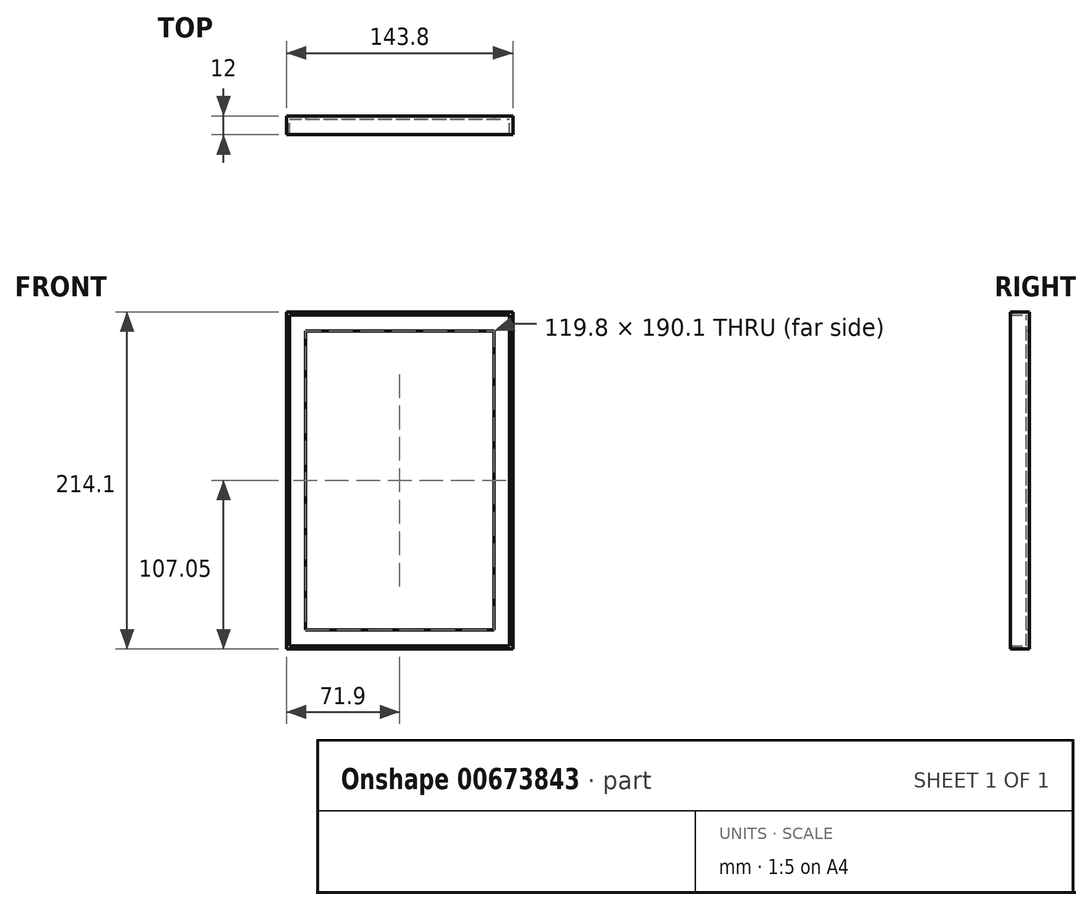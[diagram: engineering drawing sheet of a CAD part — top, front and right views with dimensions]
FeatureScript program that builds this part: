
annotation { "Feature Type Name" : "Feature", "Feature Type Description" : "" }
export const myFeature = defineFeature(function(context is Context, id is Id, definition is map)
    precondition{}
    {
        {
            var Q0;
            Q0=qCreatedBy(makeId("Front.planeOp"),FACE);
            var sketch = newSketch(context, id + "F0", { "sketchPlane" : qUnion([Q0])});
            skLineSegment(sketch, "E0.bottom", {"start": v(-145.8, -21.97) * mm, "end": v(-69, -21.97) * mm});
            skLineSegment(sketch, "E0.top", {"start": v(-145.8, 125.13) * mm, "end": v(-69, 125.13) * mm});
            skLineSegment(sketch, "E0.left", {"start": v(-145.8, -21.97) * mm, "end": v(-145.8, 125.13) * mm});
            skLineSegment(sketch, "E0.right", {"start": v(-69, -21.97) * mm, "end": v(-69, 125.13) * mm});
            skLineSegment(sketch, "E1", {"start": v(-144.8, -47.13) * mm, "end": v(-81.8, -47.13) * mm});
            skLineSegment(sketch, "E2.bottom", {"start": v(0, 0) * mm, "end": v(143.8, 0) * mm});
            skLineSegment(sketch, "E2.top", {"start": v(0, 214.1) * mm, "end": v(143.8, 214.1) * mm});
            skLineSegment(sketch, "E2.left", {"start": v(0, 0) * mm, "end": v(0, 214.1) * mm});
            skLineSegment(sketch, "E2.right", {"start": v(143.8, 0) * mm, "end": v(143.8, 214.1) * mm});
            skLineSegment(sketch, "E3.0", {"start": v(2, 212.1) * mm, "end": v(141.8, 212.1) * mm});
            skLineSegment(sketch, "E3.1", {"start": v(2, 2) * mm, "end": v(2, 212.1) * mm});
            skLineSegment(sketch, "E3.2", {"start": v(2, 2) * mm, "end": v(141.8, 2) * mm});
            skLineSegment(sketch, "E3.3", {"start": v(141.8, 2) * mm, "end": v(141.8, 212.1) * mm});
            skLineSegment(sketch, "E4", {"start": v(78.8, 212.1) * mm, "end": v(78.8, 149.1) * mm});
            skLineSegment(sketch, "E5", {"start": v(78.8, 149.1) * mm, "end": v(141.8, 149.1) * mm});
            skLineSegment(sketch, "E6", {"start": v(2, 149.1) * mm, "end": v(78.8, 149.1) * mm});
            skLineSegment(sketch, "E7", {"start": v(78.8, 149.1) * mm, "end": v(78.8, 2) * mm});
            skLineSegment(sketch, "E8.0", {"start": v(12, 202.1) * mm, "end": v(131.8, 202.1) * mm});
            skLineSegment(sketch, "E8.1", {"start": v(12, 12) * mm, "end": v(12, 202.1) * mm});
            skLineSegment(sketch, "E8.2", {"start": v(12, 12) * mm, "end": v(131.8, 12) * mm});
            skLineSegment(sketch, "E8.3", {"start": v(131.8, 12) * mm, "end": v(131.8, 202.1) * mm});
            skSolve(sketch);
        }
        {
            var Q0;
            Q0=makeQuery(id+"F0.imprint","IMPRINT",FACE,{"disambiguationData":[TD([[makeQuery(id+"F0.imprint","IMPRINT",EDGE,{"derivedFrom":sQuery(id+"F0.wireOp",EDGE,"E2.bottom")}),1.0]])]});
            extrude(context, id + "F1", {"entities" : qUnion([Q0]), "depth" : 10 * mm, "offsetDistance" : 25 * mm});
        }
        {
            var Q0;
            Q0=makeQuery(id+"F0.imprint","IMPRINT",FACE,{"disambiguationData":[TD([[makeQuery(id+"F0.imprint","IMPRINT",EDGE,{"derivedFrom":sQuery(id+"F0.wireOp",EDGE,"E2.bottom")}),1.0]])]});
            var Q1;
            {var subQ1=sQuery(id+"F0.wireOp",EDGE,"E3.1");var subQ6=sQuery(id+"F0.wireOp",EDGE,"E3.0");var subQ11=makeQuery(id+"F0.imprint","INTERSECT",VERTEX,{"derivedFrom":[subQ6,subQ1]});Q1=makeQuery(id+"F0.imprint","IMPRINT",FACE,{"disambiguationData":[TD([[makeQuery(id+"F0.imprint","IMPRINT",EDGE,{"disambiguationData":[TD([[subQ11,-1.0]])],"derivedFrom":subQ6}),-1.0]])]});}
            var Q2;
            {var subQ1=sQuery(id+"F0.wireOp",EDGE,"E3.0");var subQ5=sQuery(id+"F0.wireOp",EDGE,"E3.3");var subQ6=makeQuery(id+"F0.imprint","INTERSECT",VERTEX,{"derivedFrom":[subQ1,subQ5]});Q2=makeQuery(id+"F0.imprint","IMPRINT",FACE,{"disambiguationData":[TD([[makeQuery(id+"F0.imprint","IMPRINT",EDGE,{"disambiguationData":[TD([[subQ6,1.0]])],"derivedFrom":subQ1}),-1.0]])]});}
            var Q3;
            {var subQ1=sQuery(id+"F0.wireOp",EDGE,"E3.2");var subQ5=sQuery(id+"F0.wireOp",EDGE,"E3.1");var subQ6=makeQuery(id+"F0.imprint","INTERSECT",VERTEX,{"derivedFrom":[subQ5,subQ1]});Q3=makeQuery(id+"F0.imprint","IMPRINT",FACE,{"disambiguationData":[TD([[makeQuery(id+"F0.imprint","IMPRINT",EDGE,{"disambiguationData":[TD([[subQ6,-1.0]])],"derivedFrom":subQ5}),-1.0]])]});}
            var Q4;
            {var subQ1=sQuery(id+"F0.wireOp",EDGE,"E3.3");var subQ7=sQuery(id+"F0.wireOp",EDGE,"E3.2");var subQ8=makeQuery(id+"F0.imprint","INTERSECT",VERTEX,{"derivedFrom":[subQ7,subQ1]});Q4=makeQuery(id+"F0.imprint","IMPRINT",FACE,{"disambiguationData":[TD([[makeQuery(id+"F0.imprint","IMPRINT",EDGE,{"disambiguationData":[TD([[subQ8,1.0]])],"derivedFrom":subQ7}),1.0]])]});}
            extrude(context, id + "F2", {"entities" : qUnion([Q0, Q1, Q2, Q3, Q4]), "operationType" : NewBodyOperationType.ADD, "oppositeDirection" : true, "depth" : 2 * mm, "offsetDistance" : 25 * mm});
        }
    });
